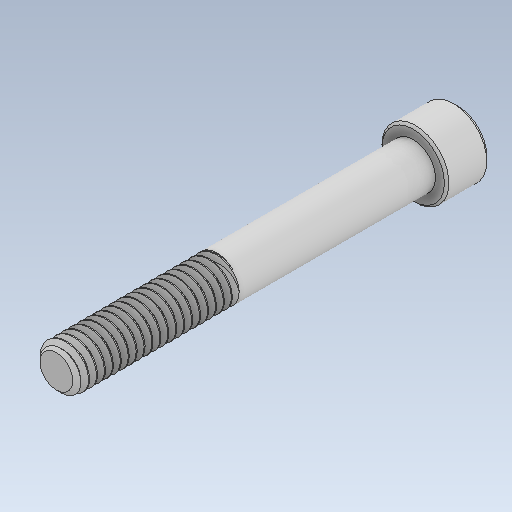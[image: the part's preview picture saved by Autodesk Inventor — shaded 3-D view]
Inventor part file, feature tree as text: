
AUTODESK INVENTOR PART (.ipt)
format: ipt  version: 2021 (Build 250183000, 183)  size: 603,648 bytes
history: native  units: in
note: dims shown in document units (in); Inventor stores cm internally (conversion verified against a paired STEP export)
features: chamfer x1
ambient origin geometry x8: Origin, YZ Plane, XZ Plane, XY Plane, X Axis, Y Axis, Z Axis, Center Point
bodies: Solid1 (feature_tree)
feature tree (1):
  chamfer  "Chamfer2"  [1 undecoded]
note: 1 required parameter value undecoded (feature->parameter linkage not recoverable at this tier; creation-order binding heuristic only, values carry confidence <= 0.55)
